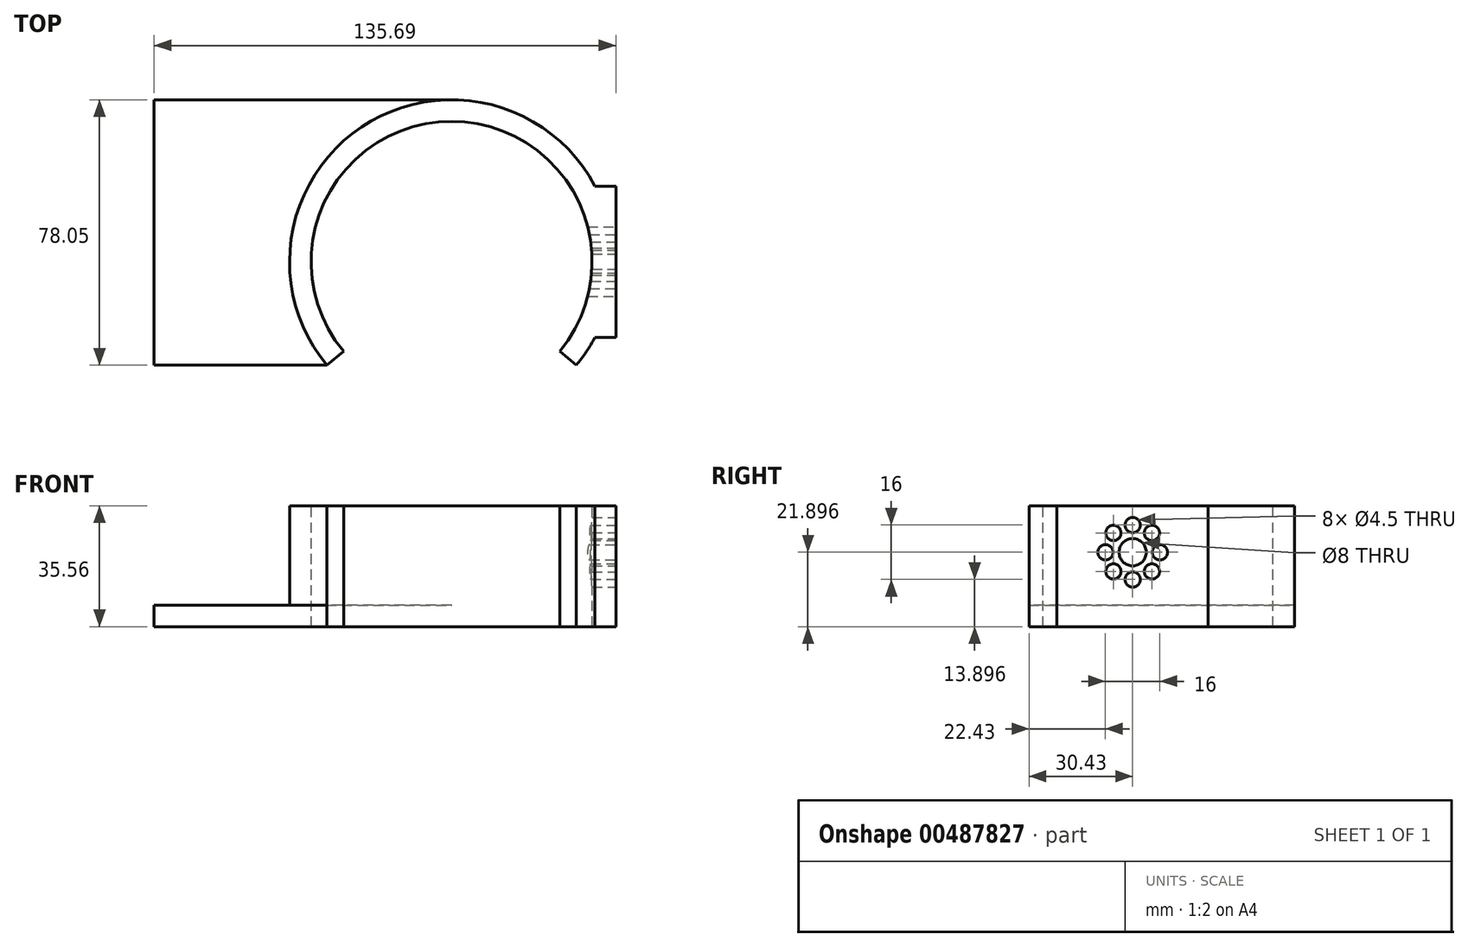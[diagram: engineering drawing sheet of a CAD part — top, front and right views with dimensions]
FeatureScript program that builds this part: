
annotation { "Feature Type Name" : "Feature", "Feature Type Description" : "" }
export const myFeature = defineFeature(function(context is Context, id is Id, definition is map)
    precondition{}
    {
        {
            var Q0;
            Q0=qCreatedBy(makeId("Top.planeOp"),FACE);
            var sketch = newSketch(context, id + "F0", { "sketchPlane" : qUnion([Q0])});
            skCircle(sketch, "E0", {"center": v(0, 0) * mm, "radius": 47.63 * mm});
            skSolve(sketch);
        }
        {
            var Q0;
            Q0 = qSketchRegion(id + "F0", true);
            extrude(context, id + "F1", {"entities" : qUnion([Q0]), "depth" : 35.56 * mm});
        }
        {
            var Q0;
            Q0=makeQuery(id+"F1.opExtrude","CAP_FACE",FACE,{"disambiguationData":[OSD([sQuery(id+"F0.wireOp",EDGE,"E0")])],"isStart":false});
            var sketch = newSketch(context, id + "F2", { "sketchPlane" : qUnion([Q0])});
            skCircle(sketch, "E1", {"center": v(0, 0) * mm, "radius": 41.28 * mm});
            skSolve(sketch);
        }
        {
            var Q0;
            Q0 = qSketchRegion(id + "F2", true);
            extrude(context, id + "F3", {"entities" : qUnion([Q0]), "operationType" : NewBodyOperationType.REMOVE, "endBound" : BoundingType.THROUGH_ALL, "oppositeDirection" : true, "depth" : 25.4 * mm});
        }
        {
            var Q0;
            Q0=qCreatedBy(makeId("Right.planeOp"),FACE);
            cPlane(context, id + "F4", {"entities" : qUnion([Q0]), "cplaneType" : CPlaneType.OFFSET, "offset" : 48.26 * mm, "width" : 152.4 * mm, "height" : 152.4 * mm});
        }
        {
            var Q0;
            Q0=qCreatedBy(id+"F4.planeOp",FACE);
            var sketch = newSketch(context, id + "F5", { "sketchPlane" : qUnion([Q0])});
            skLineSegment(sketch, "E2.bottom", {"start": v(-22.23, 0) * mm, "end": v(22.23, 0) * mm});
            skLineSegment(sketch, "E2.top", {"start": v(-22.23, 35.56) * mm, "end": v(22.23, 35.56) * mm});
            skLineSegment(sketch, "E2.left", {"start": v(-22.23, 0) * mm, "end": v(-22.23, 35.56) * mm});
            skLineSegment(sketch, "E2.right", {"start": v(22.22, 0) * mm, "end": v(22.22, 35.56) * mm});
            skPoint(sketch, "E3", {"position": v(0, 0) * mm});
            skPoint(sketch, "E4", {"position": v(0, 35.56) * mm});
            skSolve(sketch);
        }
        {
            var Q0;
            Q0 = qSketchRegion(id + "F5", true);
            var Q1;
            Q1=makeQuery(id+"F1.opExtrude","SWEPT_FACE",FACE,{"disambiguationData":[OSD([sQuery(id+"F0.wireOp",EDGE,"E0")])]});
            extrude(context, id + "F6", {"entities" : qUnion([Q0]), "operationType" : NewBodyOperationType.ADD, "endBound" : BoundingType.UP_TO_NEXT, "oppositeDirection" : true, "endBoundEntityFace" : qUnion([Q1]), "depth" : 25.4 * mm});
        }
        {
            var Q0;
            Q0=makeQuery(id+"F6.opExtrude","CAP_FACE",FACE,{"disambiguationData":[OSD([sQuery(id+"F5.wireOp",EDGE,"E2.bottom"),sQuery(id+"F5.wireOp",EDGE,"E2.top"),sQuery(id+"F5.wireOp",EDGE,"E2.left"),sQuery(id+"F5.wireOp",EDGE,"E2.right")])],"isStart":true});
            var sketch = newSketch(context, id + "F7", { "sketchPlane" : qUnion([Q0])});
            skCircle(sketch, "E5", {"center": v(0, 21.9) * mm, "radius": 8 * mm, "construction": true});
            skCircle(sketch, "E6", {"center": v(0, 29.9) * mm, "radius": 2.25 * mm});
            skCircle(sketch, "E7.1.0", {"center": v(-5.66, 27.55) * mm, "radius": 2.25 * mm});
            skCircle(sketch, "E7.2.0", {"center": v(-8, 21.9) * mm, "radius": 2.25 * mm});
            skCircle(sketch, "E7.3.0", {"center": v(-5.66, 16.24) * mm, "radius": 2.25 * mm});
            skCircle(sketch, "E7.4.0", {"center": v(0, 13.9) * mm, "radius": 2.25 * mm});
            skCircle(sketch, "E7.5.0", {"center": v(5.66, 16.24) * mm, "radius": 2.25 * mm});
            skCircle(sketch, "E7.6.0", {"center": v(8, 21.9) * mm, "radius": 2.25 * mm});
            skCircle(sketch, "E7.7.0", {"center": v(5.66, 27.55) * mm, "radius": 2.25 * mm});
            skCircle(sketch, "E8", {"center": v(0, 21.9) * mm, "radius": 4 * mm});
            skSolve(sketch);
        }
        {
            var Q0;
            Q0 = qSketchRegion(id + "F7", true);
            extrude(context, id + "F8", {"entities" : qUnion([Q0]), "operationType" : NewBodyOperationType.REMOVE, "endBound" : BoundingType.UP_TO_NEXT, "oppositeDirection" : true, "depth" : 25.4 * mm});
        }
        {
            var Q0;
            Q0=makeQuery(id+"F6.boolean.opBoolean","MERGE",FACE,{"derivedFrom":[makeQuery(id+"F1.opExtrude","CAP_FACE",FACE,{"disambiguationData":[OSD([sQuery(id+"F0.wireOp",EDGE,"E0")])],"isStart":false}),makeQuery(id+"F6.opExtrude","SWEPT_FACE",FACE,{"disambiguationData":[OSD([sQuery(id+"F5.wireOp",EDGE,"E2.top")])]})]});
            var sketch = newSketch(context, id + "F9", { "sketchPlane" : qUnion([Q0])});
            skLineSegment(sketch, "E9.bottom", {"start": v(-31.75, -26.37) * mm, "end": v(31.75, -26.37) * mm});
            skLineSegment(sketch, "E9.top", {"start": v(-65.03, -54.02) * mm, "end": v(65.03, -54.02) * mm});
            skLineSegment(sketch, "E9.left", {"start": v(-31.75, -26.37) * mm, "end": v(-65.03, -54.02) * mm});
            skLineSegment(sketch, "E9.right", {"start": v(31.75, -26.37) * mm, "end": v(65.03, -54.02) * mm});
            skPoint(sketch, "E10", {"position": v(0, -26.37) * mm});
            skSolve(sketch);
        }
        {
            var Q0;
            Q0 = qSketchRegion(id + "F9", true);
            extrude(context, id + "F10", {"entities" : qUnion([Q0]), "operationType" : NewBodyOperationType.REMOVE, "endBound" : BoundingType.THROUGH_ALL, "oppositeDirection" : true, "depth" : 25.4 * mm});
        }
        {
            var Q0;
            Q0=qCreatedBy(makeId("Top.planeOp"),FACE);
            var sketch = newSketch(context, id + "F11", { "sketchPlane" : qUnion([Q0])});
            skLineSegment(sketch, "E11.0", {"start": v(-31.75, -26.37) * mm, "end": v(-36.63, -30.43) * mm});
            skArc(sketch, "E11.1", {"start": v(0, 41.28) * mm, "mid": v(-37.36, 17.54) * mm, "end": v(-31.75, -26.37) * mm});
            skPoint(sketch, "E12", {"position": v(0, 41.28) * mm});
            skPoint(sketch, "E13.orphan", {"position": v(31.75, -26.37) * mm});
            skLineSegment(sketch, "E14", {"start": v(0, 41.28) * mm, "end": v(0, 47.63) * mm});
            skLineSegment(sketch, "E15", {"start": v(-36.63, -30.43) * mm, "end": v(-87.43, -30.43) * mm});
            skLineSegment(sketch, "E16", {"start": v(-87.43, -30.43) * mm, "end": v(-87.43, 47.63) * mm});
            skLineSegment(sketch, "E17", {"start": v(-87.43, 47.63) * mm, "end": v(0, 47.63) * mm});
            skSolve(sketch);
        }
        {
            var Q0;
            Q0 = qSketchRegion(id + "F11", true);
            extrude(context, id + "F12", {"entities" : qUnion([Q0]), "operationType" : NewBodyOperationType.ADD, "depth" : 6.35 * mm});
        }
    });
